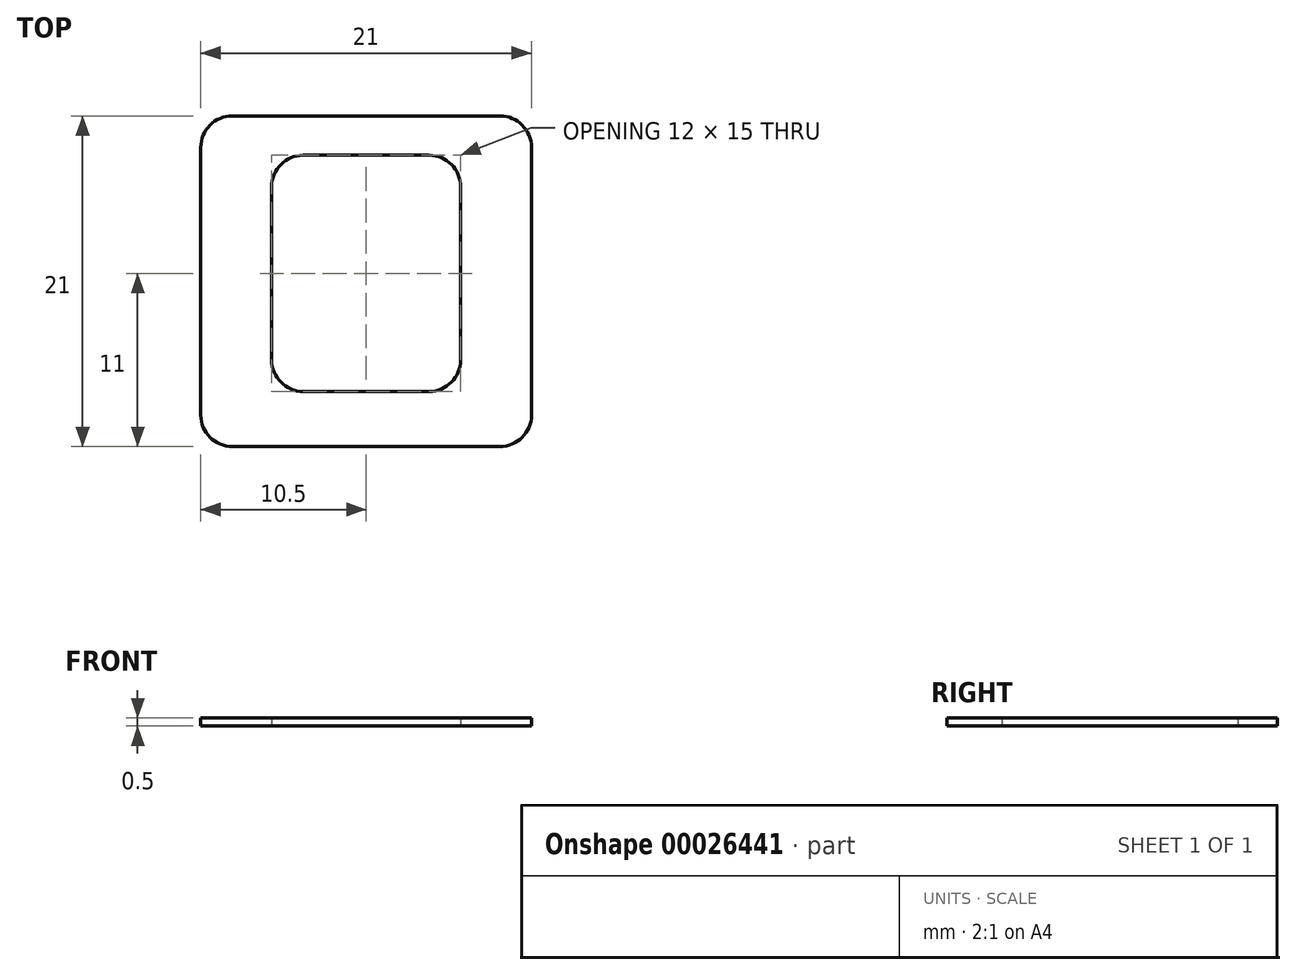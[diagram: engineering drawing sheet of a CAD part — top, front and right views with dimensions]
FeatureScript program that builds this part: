
annotation { "Feature Type Name" : "Feature", "Feature Type Description" : "" }
export const myFeature = defineFeature(function(context is Context, id is Id, definition is map)
    precondition{}
    {
        {
            var Q0;
            Q0=qCreatedBy(makeId("Top.planeOp"),FACE);
            var sketch = newSketch(context, id + "F0", { "sketchPlane" : qUnion([Q0])});
            skLineSegment(sketch, "E0.bottom", {"start": v(-8.5, 2.5) * mm, "end": v(8.5, 2.5) * mm});
            skLineSegment(sketch, "E0.top", {"start": v(-8.5, -18.5) * mm, "end": v(8.5, -18.5) * mm});
            skLineSegment(sketch, "E0.left", {"start": v(-10.5, 0.5) * mm, "end": v(-10.5, -16.5) * mm});
            skLineSegment(sketch, "E0.right", {"start": v(10.5, 0.5) * mm, "end": v(10.5, -16.5) * mm});
            skLineSegment(sketch, "E1.bottom", {"start": v(-4, 0) * mm, "end": v(4, 0) * mm});
            skLineSegment(sketch, "E1.top", {"start": v(-4, -15) * mm, "end": v(4, -15) * mm});
            skLineSegment(sketch, "E1.left", {"start": v(-6, -2) * mm, "end": v(-6, -13) * mm});
            skLineSegment(sketch, "E1.right", {"start": v(6, -2) * mm, "end": v(6, -13) * mm});
            skPoint(sketch, "E2", {"position": v(0, 0) * mm});
            skPoint(sketch, "E3", {"position": v(0, 2.5) * mm});
            skPoint(sketch, "E4.visualSharp", {"position": v(-10.5, 2.5) * mm});
            skArc(sketch, "E4.filletArc", {"start": v(-8.5, 2.5) * mm, "mid": v(-9.91, 1.91) * mm, "end": v(-10.5, 0.5) * mm});
            skPoint(sketch, "E5.visualSharp", {"position": v(-10.5, -18.5) * mm});
            skArc(sketch, "E5.filletArc", {"start": v(-10.5, -16.5) * mm, "mid": v(-9.91, -17.91) * mm, "end": v(-8.5, -18.5) * mm});
            skPoint(sketch, "E6.visualSharp", {"position": v(10.5, -18.5) * mm});
            skArc(sketch, "E6.filletArc", {"start": v(8.5, -18.5) * mm, "mid": v(9.91, -17.91) * mm, "end": v(10.5, -16.5) * mm});
            skPoint(sketch, "E7.visualSharp", {"position": v(10.5, 2.5) * mm});
            skArc(sketch, "E7.filletArc", {"start": v(10.5, 0.5) * mm, "mid": v(9.91, 1.91) * mm, "end": v(8.5, 2.5) * mm});
            skPoint(sketch, "E8.visualSharp", {"position": v(-6, 0) * mm});
            skArc(sketch, "E8.filletArc", {"start": v(-4, 0) * mm, "mid": v(-5.41, -0.59) * mm, "end": v(-6, -2) * mm});
            skPoint(sketch, "E9.visualSharp", {"position": v(-6, -15) * mm});
            skArc(sketch, "E9.filletArc", {"start": v(-6, -13) * mm, "mid": v(-5.41, -14.41) * mm, "end": v(-4, -15) * mm});
            skPoint(sketch, "E10.visualSharp", {"position": v(6, -15) * mm});
            skArc(sketch, "E10.filletArc", {"start": v(4, -15) * mm, "mid": v(5.41, -14.41) * mm, "end": v(6, -13) * mm});
            skPoint(sketch, "E11.visualSharp", {"position": v(6, 0) * mm});
            skArc(sketch, "E11.filletArc", {"start": v(6, -2) * mm, "mid": v(5.41, -0.59) * mm, "end": v(4, 0) * mm});
            skSolve(sketch);
        }
        {
            var Q0;
            Q0 = qSketchRegion(id + "F0", true);
            extrude(context, id + "F1", {"entities" : qUnion([Q0]), "depth" : 0.5 * mm});
        }
    });
